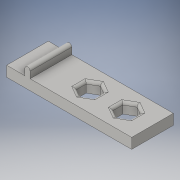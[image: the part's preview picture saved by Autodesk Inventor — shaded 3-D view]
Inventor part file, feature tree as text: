
AUTODESK INVENTOR PART (.ipt)
format: ipt  version: 2016 (Build 200138000, 138)  size: 148,480 bytes
history: native  units: in
note: dims shown in document units (in); Inventor stores cm internally (conversion verified against a paired STEP export)
features: extrude x3, sketch x3, fillet x2
ambient origin geometry x8: Origin, YZ Plane, XZ Plane, XY Plane, X Axis, Y Axis, Z Axis, Center Point
bodies: Solid1 (feature_tree)
feature tree (8):
  extrude  "Extrusion1"  Depth=6.0in
  extrude  "Extrusion2"  Depth=0.25in
  fillet  "Fillet1"  Radius=1.0in
  extrude  "Extrusion3"  Depth=0.125in TaperAngle=0.0deg
  fillet  "Fillet4"  Radius=0.125in
  sketch  "Sketch1"  dims[d0=2.0in d1=6.0in]
  sketch  "Sketch2"  dims[d2=0.5in d3=0.0in d4=0.25in d5=1.0in]
  sketch  "Sketch3"  dims[d6=2.0in d7=0.4375in d8=0.0in d9=0.125in d12=1.0in d13=1.75in d14=0.4375in d15=0.0in d16=0.125in]
